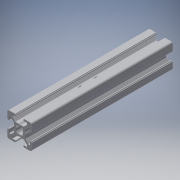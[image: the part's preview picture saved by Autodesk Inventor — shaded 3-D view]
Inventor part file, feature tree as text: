
AUTODESK INVENTOR PART (.ipt)
format: ipt  version: 2016 (Build 200138000, 138)  size: 408,064 bytes
history: native  units: in
note: dims shown in document units (in); Inventor stores cm internally (conversion verified against a paired STEP export)
features: other x3, sketch x2, extrude x1, hole x1, mirror x1
ambient origin geometry x8: Origin, YZ Plane, XZ Plane, XY Plane, X Axis, Y Axis, Z Axis, Center Point
bodies: Solid1 (feature_tree)
feature tree (8):
  other  "Blocks"
  extrude  "Extrusion1"  Depth=2.0in
  hole  "Hole1"  [1 undecoded]
  mirror  "Mirror1"
  sketch  "Sketch1"  dims[d1=0.0in d5=2.0in]
  other  "20x20"
  sketch  "Sketch3"  dims[d6=0.187in d7=0.75in d8=0.375in d9=0.25in d10=0.5635in d11=1.0in d12=0.8108in d13=1.0in d14=1.0in]
  other  "20x20:1"
note: 1 required parameter value undecoded (feature->parameter linkage not recoverable at this tier; creation-order binding heuristic only, values carry confidence <= 0.55)
